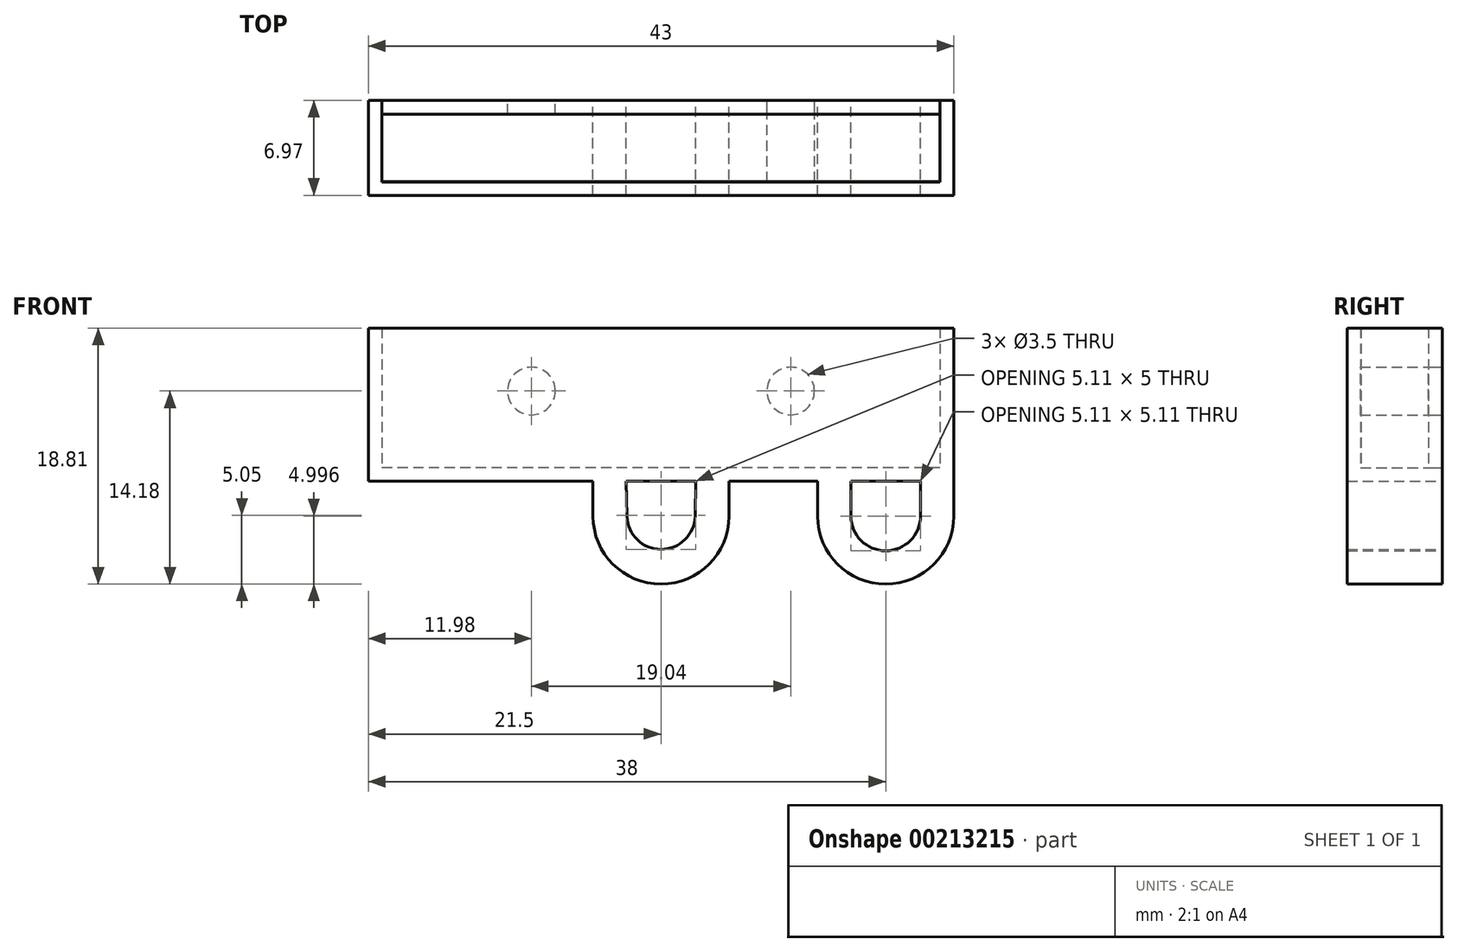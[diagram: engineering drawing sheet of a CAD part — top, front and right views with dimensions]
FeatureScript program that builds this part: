
annotation { "Feature Type Name" : "Feature", "Feature Type Description" : "" }
export const myFeature = defineFeature(function(context is Context, id is Id, definition is map)
    precondition{}
    {
        {
            var Q0;
            Q0=qCreatedBy(makeId("Front.planeOp"),FACE);
            var sketch = newSketch(context, id + "F0", { "sketchPlane" : qUnion([Q0])});
            skPoint(sketch, "E0.middle", {"position": v(0, 0) * mm});
            skLineSegment(sketch, "E1.3", {"start": v(21.5, -6.38) * mm, "end": v(-21.5, -6.38) * mm});
            skArc(sketch, "E2", {"start": v(-2.5, -8.93) * mm, "mid": v(0, -11.38) * mm, "end": v(2.5, -8.93) * mm});
            skLineSegment(sketch, "E3", {"start": v(5, -8.93) * mm, "end": v(5, -6.38) * mm});
            skLineSegment(sketch, "E4.MirrorCS", {"start": v(-5, -8.93) * mm, "end": v(-5, -6.38) * mm});
            skArc(sketch, "E5", {"start": v(-5, -8.93) * mm, "mid": v(0, -13.93) * mm, "end": v(5, -8.93) * mm});
            skLineSegment(sketch, "E6", {"start": v(2.5, -8.93) * mm, "end": v(2.55, -6.38) * mm});
            skLineSegment(sketch, "E7", {"start": v(-2.5, -8.93) * mm, "end": v(-2.55, -6.38) * mm});
            skLineSegment(sketch, "E8.0", {"start": v(20.5, -5.38) * mm, "end": v(-20.5, -5.38) * mm});
            skLineSegment(sketch, "E9.0", {"start": v(-20.5, 4.88) * mm, "end": v(-20.5, -5.38) * mm});
            skLineSegment(sketch, "E10.0", {"start": v(20.5, 4.88) * mm, "end": v(20.5, -5.38) * mm});
            skLineSegment(sketch, "E11.0", {"start": v(21.5, 4.88) * mm, "end": v(21.5, -6.38) * mm});
            skLineSegment(sketch, "E12.0", {"start": v(-21.5, 4.88) * mm, "end": v(-21.5, -6.38) * mm});
            skLineSegment(sketch, "E13.0", {"start": v(21.5, 4.88) * mm, "end": v(-21.5, 4.88) * mm});
            skLineSegment(sketch, "E14.0", {"start": v(-9.52, 4.88) * mm, "end": v(-9.52, -4.38) * mm, "construction": true});
            skCircle(sketch, "E15", {"center": v(-9.52, 0.25) * mm, "radius": 1.75 * mm});
            skCircle(sketch, "E16.MirrorC", {"center": v(9.52, 0.25) * mm, "radius": 1.75 * mm});
            skLineSegment(sketch, "E17", {"start": v(21.5, -6.38) * mm, "end": v(21.5, -8.93) * mm});
            skLineSegment(sketch, "E18.0", {"start": v(11.5, -6.38) * mm, "end": v(11.5, -8.93) * mm});
            skLineSegment(sketch, "E19.0", {"start": v(19.05, -6.38) * mm, "end": v(19.05, -8.93) * mm});
            skLineSegment(sketch, "E20.0", {"start": v(13.95, -6.38) * mm, "end": v(13.95, -8.93) * mm});
            skArc(sketch, "E21", {"start": v(13.95, -8.93) * mm, "mid": v(16.5, -11.49) * mm, "end": v(19.05, -8.93) * mm});
            skArc(sketch, "E22", {"start": v(11.5, -8.93) * mm, "mid": v(16.5, -13.93) * mm, "end": v(21.5, -8.93) * mm});
            skLineSegment(sketch, "E23.MirrorCS", {"start": v(-13.95, -6.38) * mm, "end": v(-13.95, -8.93) * mm});
            skLineSegment(sketch, "E24.MirrorCS", {"start": v(-21.5, -6.38) * mm, "end": v(-21.5, -8.93) * mm});
            skLineSegment(sketch, "E25.MirrorCS", {"start": v(-19.05, -6.38) * mm, "end": v(-19.05, -8.93) * mm});
            skLineSegment(sketch, "E26.MirrorCS", {"start": v(-11.5, -6.38) * mm, "end": v(-11.5, -8.93) * mm});
            skArc(sketch, "E27.MirrorCS", {"start": v(-11.5, -8.93) * mm, "mid": v(-16.5, -13.93) * mm, "end": v(-21.5, -8.93) * mm});
            skArc(sketch, "E28.MirrorCS", {"start": v(-13.95, -8.93) * mm, "mid": v(-16.5, -11.49) * mm, "end": v(-19.05, -8.93) * mm});
            skPoint(sketch, "E29.orphan", {"position": v(21.5, -7.3) * mm});
            skSolve(sketch);
        }
        {
            var Q0;
            Q0=makeQuery(id+"F0.imprint","IMPRINT",FACE,{"disambiguationData":[TD([[makeQuery(id+"F0.imprint","IMPRINT",EDGE,{"derivedFrom":sQuery(id+"F0.wireOp",EDGE,"E8.0")}),-1.0]])]});
            extrude(context, id + "F1", {"entities" : qUnion([Q0]), "depth" : 1 * mm});
        }
        {
            var Q0;
            Q0=makeQuery(id+"F0.imprint","IMPRINT",FACE,{"disambiguationData":[TD([[makeQuery(id+"F0.imprint","IMPRINT",EDGE,{"derivedFrom":sQuery(id+"F0.wireOp",EDGE,"e40f0d0c-a51d-45e5-ad98-77974faf851f0.MirrorCS")}),1.0]])]});
            var Q1;
            Q1=makeQuery(id+"F0.imprint","IMPRINT",FACE,{"disambiguationData":[TD([[makeQuery(id+"F0.imprint","IMPRINT",EDGE,{"derivedFrom":sQuery(id+"F0.wireOp",EDGE,"E2")}),-1.0]])]});
            var Q2;
            {var subQ4=sQuery(id+"F0.wireOp",EDGE,"ZRGvY7LQ-7EQr-ZLSA-rKNW-BgpCmVUhrDKv");Q2=makeQuery(id+"F0.imprint","IMPRINT",FACE,{"disambiguationData":[TD([[makeQuery(id+"F0.imprint","IMPRINT",EDGE,{"derivedFrom":subQ4}),-1.0]])]});}
            extrude(context, id + "F2", {"entities" : qUnion([Q0, Q1, Q2]), "depth" : 6 * mm});
        }
        {
            var Q0;
            Q0=makeQuery(id+"F0.imprint","IMPRINT",FACE,{"disambiguationData":[TD([[makeQuery(id+"F0.imprint","IMPRINT",EDGE,{"derivedFrom":sQuery(id+"F0.wireOp",EDGE,"E8.0")}),1.0]])]});
            var Q1;
            {var subQ8=sQuery(id+"F0.wireOp",EDGE,"E21");Q1=makeQuery(id+"F0.imprint","IMPRINT",FACE,{"disambiguationData":[TD([[makeQuery(id+"F0.imprint","IMPRINT",EDGE,{"derivedFrom":subQ8}),-1.0]])]});}
            var Q2;
            {var subQ3=sQuery(id+"F0.wireOp",EDGE,"E27.MirrorCS");Q2=makeQuery(id+"F0.imprint","IMPRINT",FACE,{"disambiguationData":[TD([[makeQuery(id+"F0.imprint","IMPRINT",EDGE,{"derivedFrom":subQ3}),-1.0]])]});}
            var Q3;
            Q3=makeQuery(id+"F0.imprint","IMPRINT",FACE,{"disambiguationData":[TD([[makeQuery(id+"F0.imprint","IMPRINT",EDGE,{"derivedFrom":sQuery(id+"F0.wireOp",EDGE,"E2")}),-1.0]])]});
            extrude(context, id + "F3", {"entities" : qUnion([Q0, Q1, Q2, Q3]), "depth" : 6.97 * mm});
        }
        {
            var Q0;
            Q0=makeQuery(id+"F3.opExtrude","CAP_FACE",FACE,{"disambiguationData":[OSD([sQuery(id+"F0.wireOp",EDGE,"E1.3"),sQuery(id+"F0.wireOp",EDGE,"E8.0"),sQuery(id+"F0.wireOp",EDGE,"E9.0"),sQuery(id+"F0.wireOp",EDGE,"E10.0"),sQuery(id+"F0.wireOp",EDGE,"E11.0"),sQuery(id+"F0.wireOp",EDGE,"E12.0"),sQuery(id+"F0.wireOp",EDGE,"E13.0"),sQuery(id+"F0.wireOp",EDGE,"E17"),sQuery(id+"F0.wireOp",EDGE,"E18.0"),sQuery(id+"F0.wireOp",EDGE,"E19.0"),sQuery(id+"F0.wireOp",EDGE,"E20.0"),sQuery(id+"F0.wireOp",EDGE,"E21"),sQuery(id+"F0.wireOp",EDGE,"E22"),sQuery(id+"F0.wireOp",EDGE,"E23.MirrorCS"),sQuery(id+"F0.wireOp",EDGE,"E24.MirrorCS"),sQuery(id+"F0.wireOp",EDGE,"E25.MirrorCS"),sQuery(id+"F0.wireOp",EDGE,"E26.MirrorCS"),sQuery(id+"F0.wireOp",EDGE,"E27.MirrorCS"),sQuery(id+"F0.wireOp",EDGE,"E28.MirrorCS")])],"isStart":false});
            var sketch = newSketch(context, id + "F4", { "sketchPlane" : qUnion([Q0])});
            skLineSegment(sketch, "E30.bottom", {"start": v(-20.5, 4.88) * mm, "end": v(20.5, 4.88) * mm});
            skLineSegment(sketch, "E30.top", {"start": v(-20.5, -5.38) * mm, "end": v(20.5, -5.38) * mm});
            skLineSegment(sketch, "E30.left", {"start": v(-20.5, 4.88) * mm, "end": v(-20.5, -5.38) * mm});
            skLineSegment(sketch, "E30.right", {"start": v(20.5, 4.88) * mm, "end": v(20.5, -5.38) * mm});
            skSolve(sketch);
        }
        {
            var Q0;
            Q0=makeQuery(id+"F4.imprint","IMPRINT",FACE,{"disambiguationData":[TD([[makeQuery(id+"F4.imprint","IMPRINT",EDGE,{"derivedFrom":sQuery(id+"F4.wireOp",EDGE,"E30.bottom")}),-1.0]])]});
            extrude(context, id + "F5", {"entities" : qUnion([Q0]), "operationType" : NewBodyOperationType.ADD, "oppositeDirection" : true, "depth" : 1 * mm});
        }
        {
            var Q0;
            Q0=makeQuery(id+"F2.opExtrude","SWEPT_BODY",BODY,{"disambiguationData":[OSD([sQuery(id+"F0.wireOp",EDGE,"E1.3"),sQuery(id+"F0.wireOp",EDGE,"E2"),sQuery(id+"F0.wireOp",EDGE,"E3"),sQuery(id+"F0.wireOp",EDGE,"E4.MirrorCS"),sQuery(id+"F0.wireOp",EDGE,"E5"),sQuery(id+"F0.wireOp",EDGE,"E6"),sQuery(id+"F0.wireOp",EDGE,"E7")])]});
            deleteBodies(context, id + "F6", {"entities" : qUnion([Q0])});
        }
        {
            var Q0;
            Q0=makeQuery(id+"F0.imprint","IMPRINT",FACE,{"disambiguationData":[TD([[makeQuery(id+"F0.imprint","IMPRINT",EDGE,{"derivedFrom":sQuery(id+"F0.wireOp",EDGE,"E16.MirrorC")}),-1.0]])]});
            var Q1;
            Q1=makeQuery(id+"F0.imprint","IMPRINT",FACE,{"disambiguationData":[TD([[makeQuery(id+"F0.imprint","IMPRINT",EDGE,{"derivedFrom":sQuery(id+"F0.wireOp",EDGE,"E15")}),1.0]])]});
            extrude(context, id + "F7", {"entities" : qUnion([Q0, Q1]), "depth" : 6 * mm});
        }
    });
